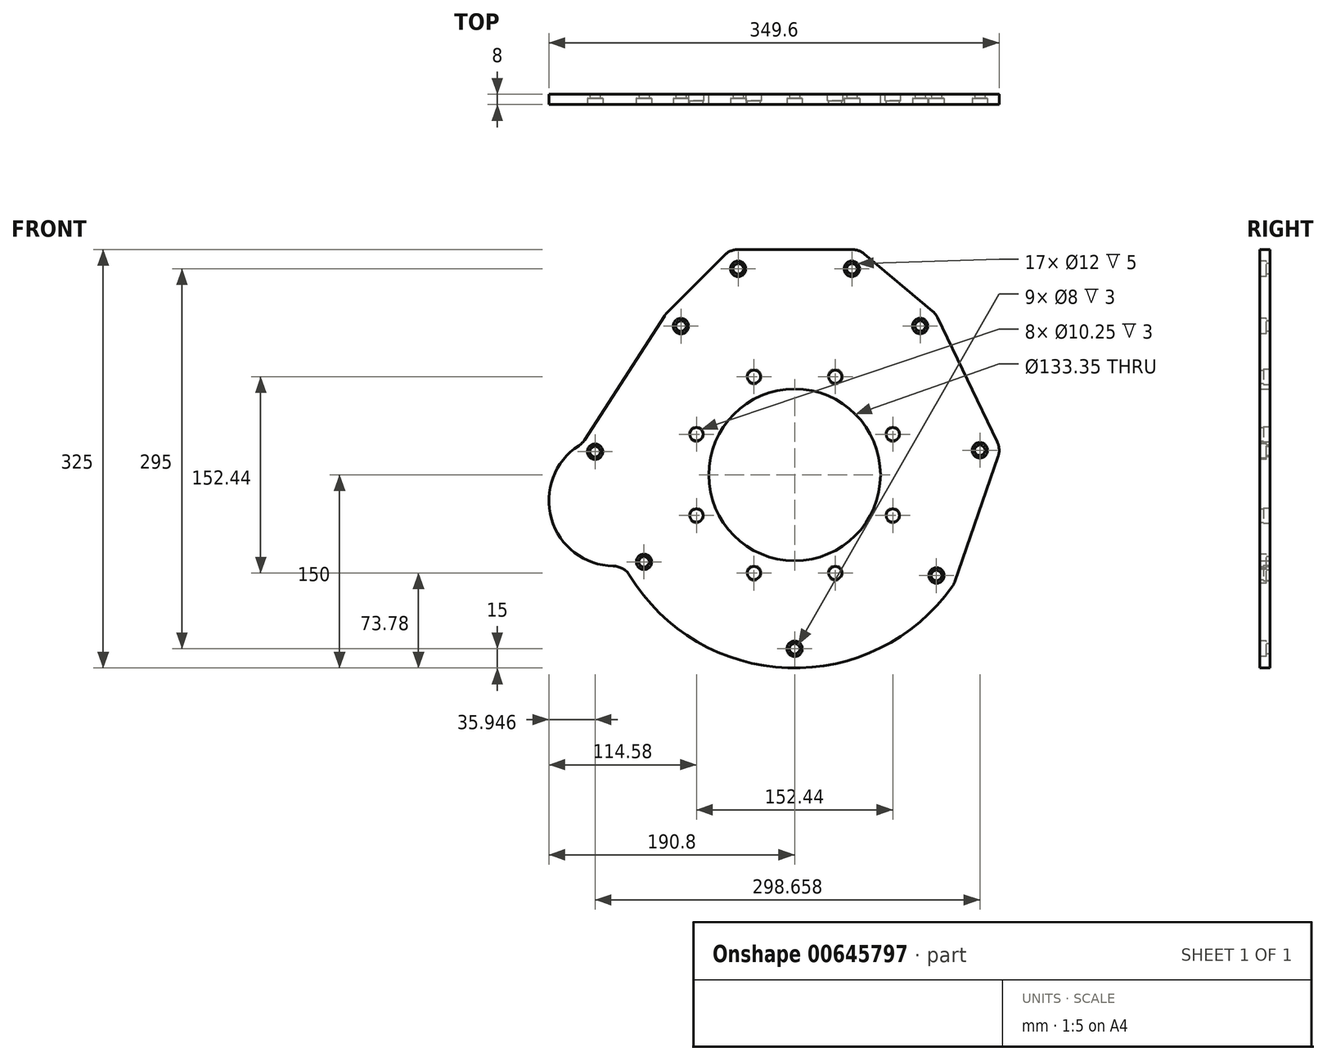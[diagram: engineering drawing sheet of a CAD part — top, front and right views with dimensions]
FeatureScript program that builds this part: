
annotation { "Feature Type Name" : "Feature", "Feature Type Description" : "" }
export const myFeature = defineFeature(function(context is Context, id is Id, definition is map)
    precondition{}
    {
        {
            var Q0;
            Q0=qCreatedBy(makeId("Front.planeOp"),FACE);
            var sketch = newSketch(context, id + "F0", { "sketchPlane" : qUnion([Q0])});
            skLineSegment(sketch, "E0", {"start": v(-50, 175) * mm, "end": v(50, 175) * mm});
            skLineSegment(sketch, "E1", {"start": v(50, 175) * mm, "end": v(109.59, 125) * mm});
            skLineSegment(sketch, "E2", {"start": v(109.59, 125) * mm, "end": v(160, 20) * mm});
            skLineSegment(sketch, "E3", {"start": v(-165, 24.22) * mm, "end": v(-100, 125) * mm});
            skLineSegment(sketch, "E4", {"start": v(-100, 125) * mm, "end": v(-50, 175) * mm});
            skLineSegment(sketch, "E5", {"start": v(0, 175) * mm, "end": v(0, 0) * mm, "construction": true});
            skArc(sketch, "E6", {"start": v(-165, 24.22) * mm, "mid": v(-188.04, -36.51) * mm, "end": v(-132.53, -70.25) * mm});
            skArc(sketch, "E7", {"start": v(-132.53, -70.25) * mm, "mid": v(-8.63, -149.75) * mm, "end": v(123.6, -85) * mm});
            skLineSegment(sketch, "E8", {"start": v(160, 20) * mm, "end": v(123.6, -85) * mm});
            skCircle(sketch, "E9", {"center": v(0, 0) * mm, "radius": 66.68 * mm});
            skSolve(sketch);
        }
        {
            var Q0;
            Q0=qSketchRegion(id+"F0",true);
            extrude(context, id + "F1", {"entities" : qUnion([Q0]), "depth" : 8 * mm});
        }
        {
            var Q0;
            Q0=makeQuery(id+"F1.opExtrude","CAP_FACE",FACE,{"disambiguationData":[OSD([sQuery(id+"F0.wireOp",EDGE,"E0"),sQuery(id+"F0.wireOp",EDGE,"E1"),sQuery(id+"F0.wireOp",EDGE,"E2"),sQuery(id+"F0.wireOp",EDGE,"E3"),sQuery(id+"F0.wireOp",EDGE,"E4"),sQuery(id+"F0.wireOp",EDGE,"E6"),sQuery(id+"F0.wireOp",EDGE,"E7"),sQuery(id+"F0.wireOp",EDGE,"E8"),sQuery(id+"F0.wireOp",EDGE,"E9")])],"isStart":true});
            var sketch = newSketch(context, id + "F2", { "sketchPlane" : qUnion([Q0])});
            skCircle(sketch, "E10", {"center": v(0, 0) * mm, "radius": 82.5 * mm, "construction": true});
            skCircle(sketch, "E11", {"center": v(-31.57, 76.22) * mm, "radius": 5.12 * mm});
            skCircle(sketch, "E12.1.0", {"center": v(-76.22, 31.57) * mm, "radius": 5.12 * mm});
            skCircle(sketch, "E12.2.0", {"center": v(-76.22, -31.57) * mm, "radius": 5.12 * mm});
            skCircle(sketch, "E12.3.0", {"center": v(-31.57, -76.22) * mm, "radius": 5.12 * mm});
            skCircle(sketch, "E12.4.0", {"center": v(31.57, -76.22) * mm, "radius": 5.12 * mm});
            skCircle(sketch, "E12.5.0", {"center": v(76.22, -31.57) * mm, "radius": 5.12 * mm});
            skCircle(sketch, "E12.6.0", {"center": v(76.22, 31.57) * mm, "radius": 5.12 * mm});
            skCircle(sketch, "E12.7.0", {"center": v(31.57, 76.22) * mm, "radius": 5.12 * mm});
            skLineSegment(sketch, "E13", {"start": v(-31.57, 76.22) * mm, "end": v(0, 0) * mm, "construction": true});
            skLineSegment(sketch, "E14", {"start": v(0, 0) * mm, "end": v(0, 82.5) * mm, "construction": true});
            skSolve(sketch);
        }
        {
            var Q0;
            Q0=sQuery(id+"F2.wireOp",VERTEX,"E11.center");
            var Q1;
            Q1=sQuery(id+"F2.wireOp",VERTEX,"E12.7.0.center");
            var Q2;
            Q2=sQuery(id+"F2.wireOp",VERTEX,"E12.6.0.center");
            var Q3;
            Q3=sQuery(id+"F2.wireOp",VERTEX,"E12.5.0.center");
            var Q4;
            Q4=sQuery(id+"F2.wireOp",VERTEX,"E12.4.0.center");
            var Q5;
            Q5=sQuery(id+"F2.wireOp",VERTEX,"E12.3.0.center");
            var Q6;
            Q6=sQuery(id+"F2.wireOp",VERTEX,"E12.2.0.center");
            var Q7;
            Q7=sQuery(id+"F2.wireOp",VERTEX,"E12.1.0.center");
            var Q8;
            Q8=makeQuery(id+"F1.opExtrude","SWEPT_BODY",BODY,{"disambiguationData":[OSD([sQuery(id+"F0.wireOp",EDGE,"E0"),sQuery(id+"F0.wireOp",EDGE,"E1"),sQuery(id+"F0.wireOp",EDGE,"E2"),sQuery(id+"F0.wireOp",EDGE,"E3"),sQuery(id+"F0.wireOp",EDGE,"E4"),sQuery(id+"F0.wireOp",EDGE,"E6"),sQuery(id+"F0.wireOp",EDGE,"E7"),sQuery(id+"F0.wireOp",EDGE,"E8"),sQuery(id+"F0.wireOp",EDGE,"E9")])]});
            hole(context, id + "F3", {"style" : HoleStyle.C_BORE, "holeDiameter" : 8 * mm, "cBoreDiameter" : 12 * mm, "cBoreDepth" : 5 * mm, "endStyle" : HoleEndStyle.THROUGH, "locations" : qUnion([Q0, Q1, Q2, Q3, Q4, Q5, Q6, Q7]), "scope" : qUnion([Q8])});
        }
        {
            var Q0;
            Q0=makeQuery(id+"F1.opExtrude","SWEPT_EDGE",EDGE,{"disambiguationData":[OSD([sQuery(id+"F0.wireOp",EDGE,"E2"),sQuery(id+"F0.wireOp",EDGE,"E8")])]});
            var Q1;
            Q1=makeQuery(id+"F1.opExtrude","SWEPT_EDGE",EDGE,{"disambiguationData":[OSD([sQuery(id+"F0.wireOp",EDGE,"E1"),sQuery(id+"F0.wireOp",EDGE,"E2")])]});
            var Q2;
            Q2=makeQuery(id+"F1.opExtrude","SWEPT_EDGE",EDGE,{"disambiguationData":[OSD([sQuery(id+"F0.wireOp",EDGE,"E0"),sQuery(id+"F0.wireOp",EDGE,"E1")])]});
            var Q3;
            Q3=makeQuery(id+"F1.opExtrude","SWEPT_EDGE",EDGE,{"disambiguationData":[OSD([sQuery(id+"F0.wireOp",EDGE,"E0"),sQuery(id+"F0.wireOp",EDGE,"E4")])]});
            var Q4;
            Q4=makeQuery(id+"F1.opExtrude","SWEPT_EDGE",EDGE,{"disambiguationData":[OSD([sQuery(id+"F0.wireOp",EDGE,"E3"),sQuery(id+"F0.wireOp",EDGE,"E4")])]});
            var Q5;
            Q5=makeQuery(id+"F1.opExtrude","SWEPT_EDGE",EDGE,{"disambiguationData":[OSD([sQuery(id+"F0.wireOp",EDGE,"E3"),sQuery(id+"F0.wireOp",EDGE,"E6")])]});
            var Q6;
            Q6=makeQuery(id+"F1.opExtrude","SWEPT_EDGE",EDGE,{"disambiguationData":[OSD([sQuery(id+"F0.wireOp",EDGE,"E6"),sQuery(id+"F0.wireOp",EDGE,"E7")])]});
            var Q7;
            Q7=makeQuery(id+"F1.opExtrude","SWEPT_EDGE",EDGE,{"disambiguationData":[OSD([sQuery(id+"F0.wireOp",EDGE,"E7"),sQuery(id+"F0.wireOp",EDGE,"E8")])]});
            fillet(context, id + "F4", {"entities" : qUnion([Q0, Q1, Q2, Q3, Q4, Q5, Q6, Q7]), "radius" : 15 * mm, "tangentPropagation" : true, "allowEdgeOverflow" : false});
        }
        {
            var Q0;
            Q0=makeQuery(id+"F1.opExtrude","CAP_FACE",FACE,{"disambiguationData":[OSD([sQuery(id+"F0.wireOp",EDGE,"E0"),sQuery(id+"F0.wireOp",EDGE,"E1"),sQuery(id+"F0.wireOp",EDGE,"E2"),sQuery(id+"F0.wireOp",EDGE,"E3"),sQuery(id+"F0.wireOp",EDGE,"E4"),sQuery(id+"F0.wireOp",EDGE,"E6"),sQuery(id+"F0.wireOp",EDGE,"E7"),sQuery(id+"F0.wireOp",EDGE,"E8"),sQuery(id+"F0.wireOp",EDGE,"E9")])],"isStart":false});
            var sketch = newSketch(context, id + "F5", { "sketchPlane" : qUnion([Q0])});
            skPoint(sketch, "E15", {"position": v(-43.79, 160) * mm});
            skPoint(sketch, "E16", {"position": v(44.54, 160) * mm});
            skPoint(sketch, "E17", {"position": v(97.47, 115.59) * mm});
            skPoint(sketch, "E18", {"position": v(143.8, 19.08) * mm});
            skPoint(sketch, "E19", {"position": v(110.1, -78.12) * mm});
            skPoint(sketch, "E20", {"position": v(0, -135) * mm});
            skPoint(sketch, "E21", {"position": v(-116.91, -67.5) * mm});
            skPoint(sketch, "E22", {"position": v(-154.85, 18) * mm});
            skPoint(sketch, "E23", {"position": v(-88.26, 115.52) * mm});
            skCircle(sketch, "E24", {"center": v(0, 0) * mm, "radius": 135 * mm, "construction": true});
            skLineSegment(sketch, "E25", {"start": v(0, 0) * mm, "end": v(-116.91, -67.5) * mm, "construction": true});
            skLineSegment(sketch, "E26", {"start": v(0, 0) * mm, "end": v(0, -135) * mm, "construction": true});
            skCircle(sketch, "E27", {"center": v(-140, -20) * mm, "radius": 40.8 * mm, "construction": true});
            skSolve(sketch);
        }
        {
            var Q0;
            Q0=sQuery(id+"F5.wireOp",VERTEX,"E15");
            var Q1;
            Q1=sQuery(id+"F5.wireOp",VERTEX,"E23");
            var Q2;
            Q2=sQuery(id+"F5.wireOp",VERTEX,"E22");
            var Q3;
            Q3=sQuery(id+"F5.wireOp",VERTEX,"E21");
            var Q4;
            Q4=sQuery(id+"F5.wireOp",VERTEX,"E20");
            var Q5;
            Q5=sQuery(id+"F5.wireOp",VERTEX,"E19");
            var Q6;
            Q6=sQuery(id+"F5.wireOp",VERTEX,"E18");
            var Q7;
            Q7=sQuery(id+"F5.wireOp",VERTEX,"E17");
            var Q8;
            Q8=sQuery(id+"F5.wireOp",VERTEX,"E16");
            var Q9;
            Q9=makeQuery(id+"F1.opExtrude","SWEPT_BODY",BODY,{"disambiguationData":[OSD([sQuery(id+"F0.wireOp",EDGE,"E0"),sQuery(id+"F0.wireOp",EDGE,"E1"),sQuery(id+"F0.wireOp",EDGE,"E2"),sQuery(id+"F0.wireOp",EDGE,"E3"),sQuery(id+"F0.wireOp",EDGE,"E4"),sQuery(id+"F0.wireOp",EDGE,"E6"),sQuery(id+"F0.wireOp",EDGE,"E7"),sQuery(id+"F0.wireOp",EDGE,"E8"),sQuery(id+"F0.wireOp",EDGE,"E9")])]});
            hole(context, id + "F6", {"style" : HoleStyle.C_BORE, "holeDiameter" : 8 * mm, "cBoreDiameter" : 12 * mm, "cBoreDepth" : 5 * mm, "endStyle" : HoleEndStyle.THROUGH, "locations" : qUnion([Q0, Q1, Q2, Q3, Q4, Q5, Q6, Q7, Q8]), "scope" : qUnion([Q9])});
        }
        {
            var Q0;
            Q0=qSketchRegion(id+"F2",true);
            extrude(context, id + "F7", {"entities" : qUnion([Q0]), "operationType" : NewBodyOperationType.REMOVE, "endBound" : BoundingType.THROUGH_ALL, "oppositeDirection" : true, "depth" : 25 * mm});
        }
    });
